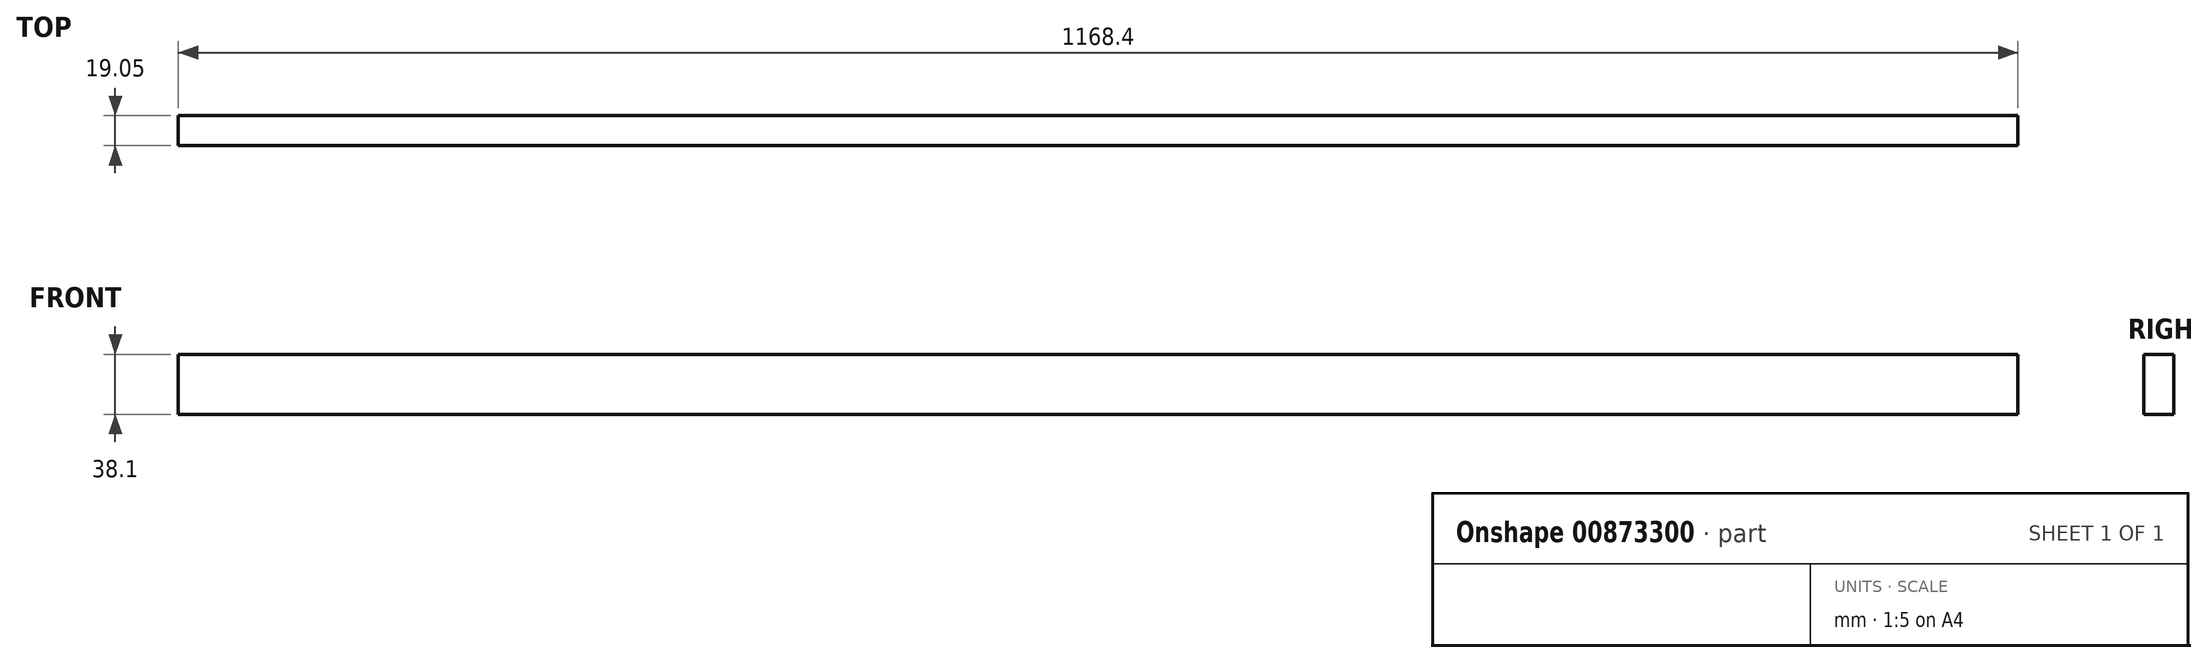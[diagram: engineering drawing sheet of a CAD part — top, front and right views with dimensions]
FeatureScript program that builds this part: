
annotation { "Feature Type Name" : "Feature", "Feature Type Description" : "" }
export const myFeature = defineFeature(function(context is Context, id is Id, definition is map)
    precondition{}
    {
        {
            var Q0;
            Q0=qCreatedBy(makeId("Front.planeOp"),FACE);
            var sketch = newSketch(context, id + "F0", { "sketchPlane" : qUnion([Q0])});
            skLineSegment(sketch, "E0.bottom", {"start": v(0, 0) * mm, "end": v(-1168.4, 0) * mm});
            skLineSegment(sketch, "E0.top", {"start": v(0, 38.1) * mm, "end": v(-1168.4, 38.1) * mm});
            skLineSegment(sketch, "E0.left", {"start": v(0, 0) * mm, "end": v(0, 38.1) * mm});
            skLineSegment(sketch, "E0.right", {"start": v(-1168.4, 0) * mm, "end": v(-1168.4, 38.1) * mm});
            skSolve(sketch);
        }
        {
            var Q0;
            Q0=makeQuery(id+"F0.imprint","IMPRINT",FACE,{"disambiguationData":[TD([[makeQuery(id+"F0.imprint","IMPRINT",EDGE,{"derivedFrom":sQuery(id+"F0.wireOp",EDGE,"E0.bottom")}),-1.0]])]});
            extrude(context, id + "F1", {"entities" : qUnion([Q0]), "depth" : 19.05 * mm, "offsetDistance" : 25.4 * mm});
        }
    });
